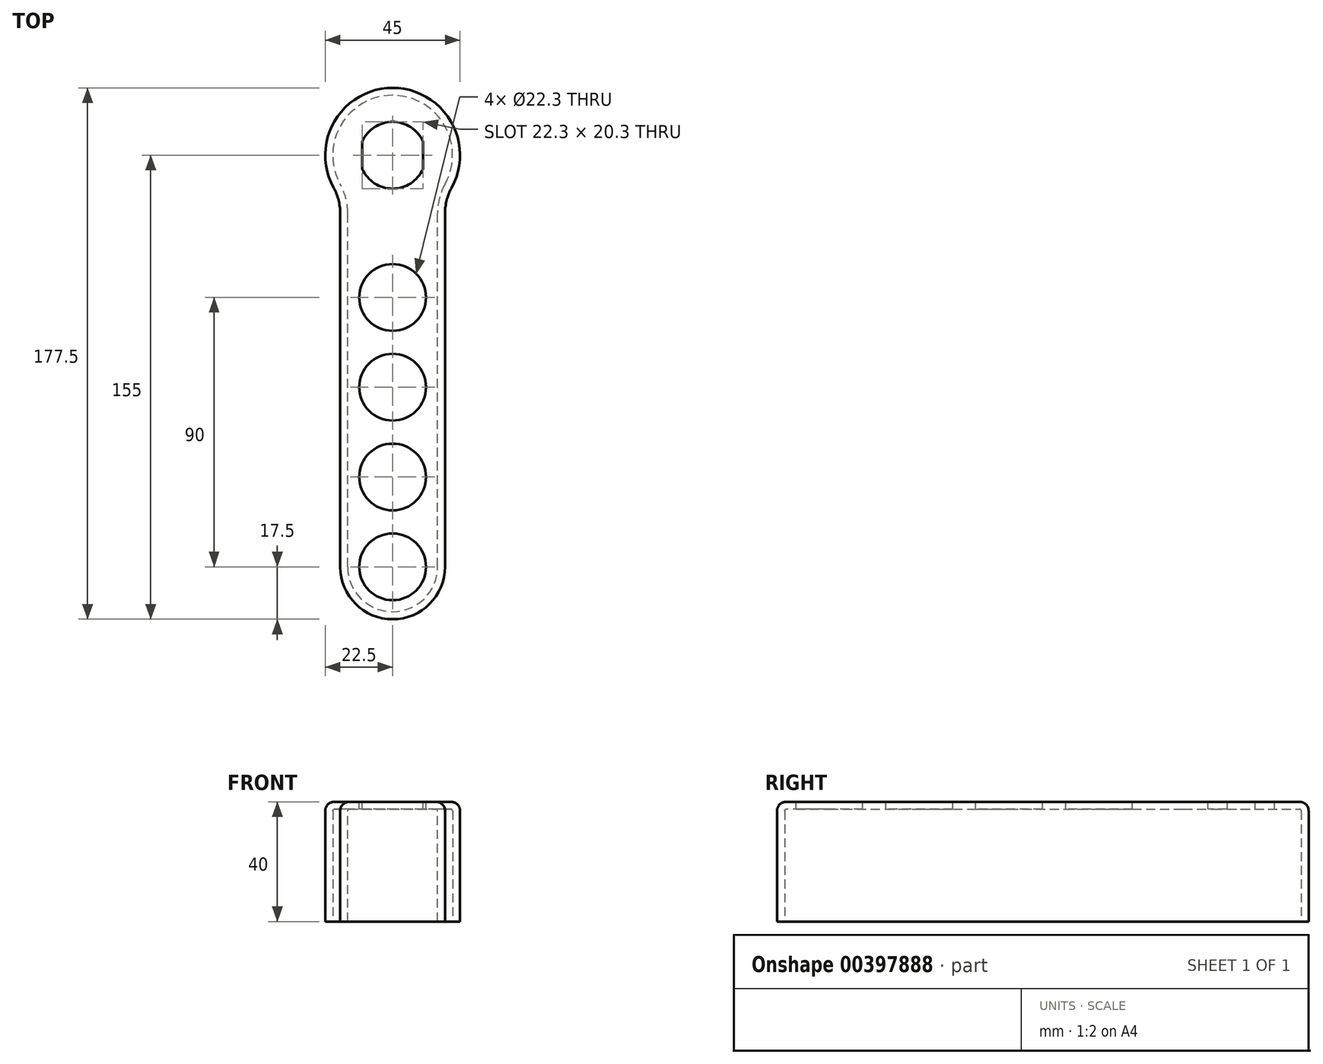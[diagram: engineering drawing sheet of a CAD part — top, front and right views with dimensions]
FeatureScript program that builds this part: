
annotation { "Feature Type Name" : "Feature", "Feature Type Description" : "" }
export const myFeature = defineFeature(function(context is Context, id is Id, definition is map)
    precondition{}
    {
        {
            var Q0;
            Q0=qCreatedBy(makeId("Top.planeOp"),FACE);
            var sketch = newSketch(context, id + "F0", { "sketchPlane" : qUnion([Q0])});
            skLineSegment(sketch, "E0.bottom", {"start": v(0, 0) * mm, "end": v(35, 0) * mm});
            skLineSegment(sketch, "E0.top", {"start": v(0, 155) * mm, "end": v(35, 155) * mm});
            skLineSegment(sketch, "E0.left", {"start": v(0, 0) * mm, "end": v(0, 155) * mm});
            skLineSegment(sketch, "E0.right", {"start": v(35, 0) * mm, "end": v(35, 155) * mm});
            skCircle(sketch, "E1", {"center": v(17.5, 155) * mm, "radius": 22.5 * mm});
            skSolve(sketch);
        }
        {
            var Q0;
            Q0 = qSketchRegion(id + "F0", true);
            extrude(context, id + "F1", {"entities" : qUnion([Q0]), "depth" : 40 * mm});
        }
        {
            var Q0;
            Q0=makeQuery(id+"F1.opExtrude","SWEPT_EDGE",EDGE,{"disambiguationData":[OSD([sQuery(id+"F0.wireOp",EDGE,"E0.bottom"),sQuery(id+"F0.wireOp",EDGE,"E0.right")])]});
            var Q1;
            Q1=makeQuery(id+"F1.opExtrude","SWEPT_EDGE",EDGE,{"disambiguationData":[OSD([sQuery(id+"F0.wireOp",EDGE,"E0.bottom"),sQuery(id+"F0.wireOp",EDGE,"E0.left")])]});
            var Q2;
            Q2=makeQuery(id+"F1.opExtrude","SWEPT_EDGE",EDGE,{"disambiguationData":[OSD([sQuery(id+"F0.wireOp",EDGE,"E0.right"),sQuery(id+"F0.wireOp",EDGE,"E1")])]});
            var Q3;
            Q3=makeQuery(id+"F1.opExtrude","SWEPT_EDGE",EDGE,{"disambiguationData":[OSD([sQuery(id+"F0.wireOp",EDGE,"E0.left"),sQuery(id+"F0.wireOp",EDGE,"E1")])]});
            fillet(context, id + "F2", {"entities" : qUnion([Q0, Q1, Q2, Q3]), "radius" : 17.5 * mm, "tangentPropagation" : true, "allowEdgeOverflow" : false});
        }
        {
            var Q0;
            Q0=makeQuery(id+"F1.opExtrude","CAP_FACE",FACE,{"disambiguationData":[OSD([sQuery(id+"F0.wireOp",EDGE,"E0.bottom"),sQuery(id+"F0.wireOp",EDGE,"E0.left"),sQuery(id+"F0.wireOp",EDGE,"E0.right"),sQuery(id+"F0.wireOp",EDGE,"E1")])],"isStart":false});
            fillet(context, id + "F3", {"entities" : qUnion([Q0]), "radius" : 3 * mm, "tangentPropagation" : true, "allowEdgeOverflow" : false});
        }
        {
            var Q0;
            Q0=makeQuery(id+"F1.opExtrude","CAP_FACE",FACE,{"disambiguationData":[OSD([sQuery(id+"F0.wireOp",EDGE,"E0.bottom"),sQuery(id+"F0.wireOp",EDGE,"E0.left"),sQuery(id+"F0.wireOp",EDGE,"E0.right"),sQuery(id+"F0.wireOp",EDGE,"E1")])],"isStart":true});
            shell(context, id + "F4", {"entities" : qUnion([Q0]), "thickness" : 2.5 * mm});
        }
        {
            var Q0;
            Q0=makeQuery(id+"F1.opExtrude","CAP_FACE",FACE,{"disambiguationData":[OSD([sQuery(id+"F0.wireOp",EDGE,"E0.bottom"),sQuery(id+"F0.wireOp",EDGE,"E0.left"),sQuery(id+"F0.wireOp",EDGE,"E0.right"),sQuery(id+"F0.wireOp",EDGE,"E1")])],"isStart":false});
            var sketch = newSketch(context, id + "F5", { "sketchPlane" : qUnion([Q0])});
            skCircle(sketch, "E2", {"center": v(17.5, 17.5) * mm, "radius": 11.15 * mm});
            skCircle(sketch, "E3", {"center": v(17.5, 47.5) * mm, "radius": 11.15 * mm});
            skCircle(sketch, "E4", {"center": v(17.5, 77.5) * mm, "radius": 11.15 * mm});
            skCircle(sketch, "E5", {"center": v(17.5, 107.5) * mm, "radius": 11.15 * mm});
            skCircle(sketch, "E6", {"center": v(17.5, 155) * mm, "radius": 11.15 * mm});
            skLineSegment(sketch, "E7", {"start": v(27.65, 150.38) * mm, "end": v(27.65, 159.62) * mm});
            skLineSegment(sketch, "E8", {"start": v(7.35, 150.38) * mm, "end": v(7.35, 159.62) * mm});
            skSolve(sketch);
        }
        {
            var Q0;
            Q0=makeQuery(id+"F5.imprint","IMPRINT",FACE,{"disambiguationData":[TD([[makeQuery(id+"F5.imprint","IMPRINT",EDGE,{"derivedFrom":sQuery(id+"F5.wireOp",EDGE,"E2")}),1.0]])]});
            var Q1;
            Q1=makeQuery(id+"F5.imprint","IMPRINT",FACE,{"disambiguationData":[TD([[makeQuery(id+"F5.imprint","IMPRINT",EDGE,{"derivedFrom":sQuery(id+"F5.wireOp",EDGE,"E3")}),1.0]])]});
            var Q2;
            Q2=makeQuery(id+"F5.imprint","IMPRINT",FACE,{"disambiguationData":[TD([[makeQuery(id+"F5.imprint","IMPRINT",EDGE,{"derivedFrom":sQuery(id+"F5.wireOp",EDGE,"E4")}),1.0]])]});
            var Q3;
            Q3=makeQuery(id+"F5.imprint","IMPRINT",FACE,{"disambiguationData":[TD([[makeQuery(id+"F5.imprint","IMPRINT",EDGE,{"derivedFrom":sQuery(id+"F5.wireOp",EDGE,"E5")}),1.0]])]});
            var Q4;
            {var subQ0=sQuery(id+"F5.wireOp",EDGE,"E7");Q4=makeQuery(id+"F5.imprint","IMPRINT",FACE,{"disambiguationData":[TD([[makeQuery(id+"F5.imprint","IMPRINT",EDGE,{"derivedFrom":subQ0}),1.0]])]});}
            extrude(context, id + "F6", {"entities" : qUnion([Q0, Q1, Q2, Q3, Q4]), "operationType" : NewBodyOperationType.REMOVE, "endBound" : BoundingType.THROUGH_ALL, "oppositeDirection" : true, "depth" : 25 * mm});
        }
    });
